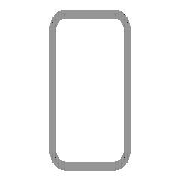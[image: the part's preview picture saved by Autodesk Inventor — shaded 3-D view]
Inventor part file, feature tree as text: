
AUTODESK INVENTOR PART (.ipt)
format: ipt  version: 2025 (Build 290162010, 162A)  size: 129,024 bytes
history: native  units: mm (DEFAULTED — no unit token found)
features: other x3, sketch x1, plane x1
ambient origin geometry x8: Origin, YZ Plane, XZ Plane, XY Plane, X Axis, Y Axis, Z Axis, Center Point
bodies: Solid1 (feature_tree), Body (feature_tree)
feature tree (5):
  other  "Driven Length"
  other  "Start plane"
  other  "End plane"
  sketch  "Sketch3"  dims[d3=740.0mm d4=0.0mm d7=4.0mm d9=40.0mm d11=80.0mm d12=2.0mm d13=-0.0mm d14=740.0mm d15=20.0mm d16=40.0mm d17=90.0deg d18=740.0mm]
  plane  "Work Plane3"
